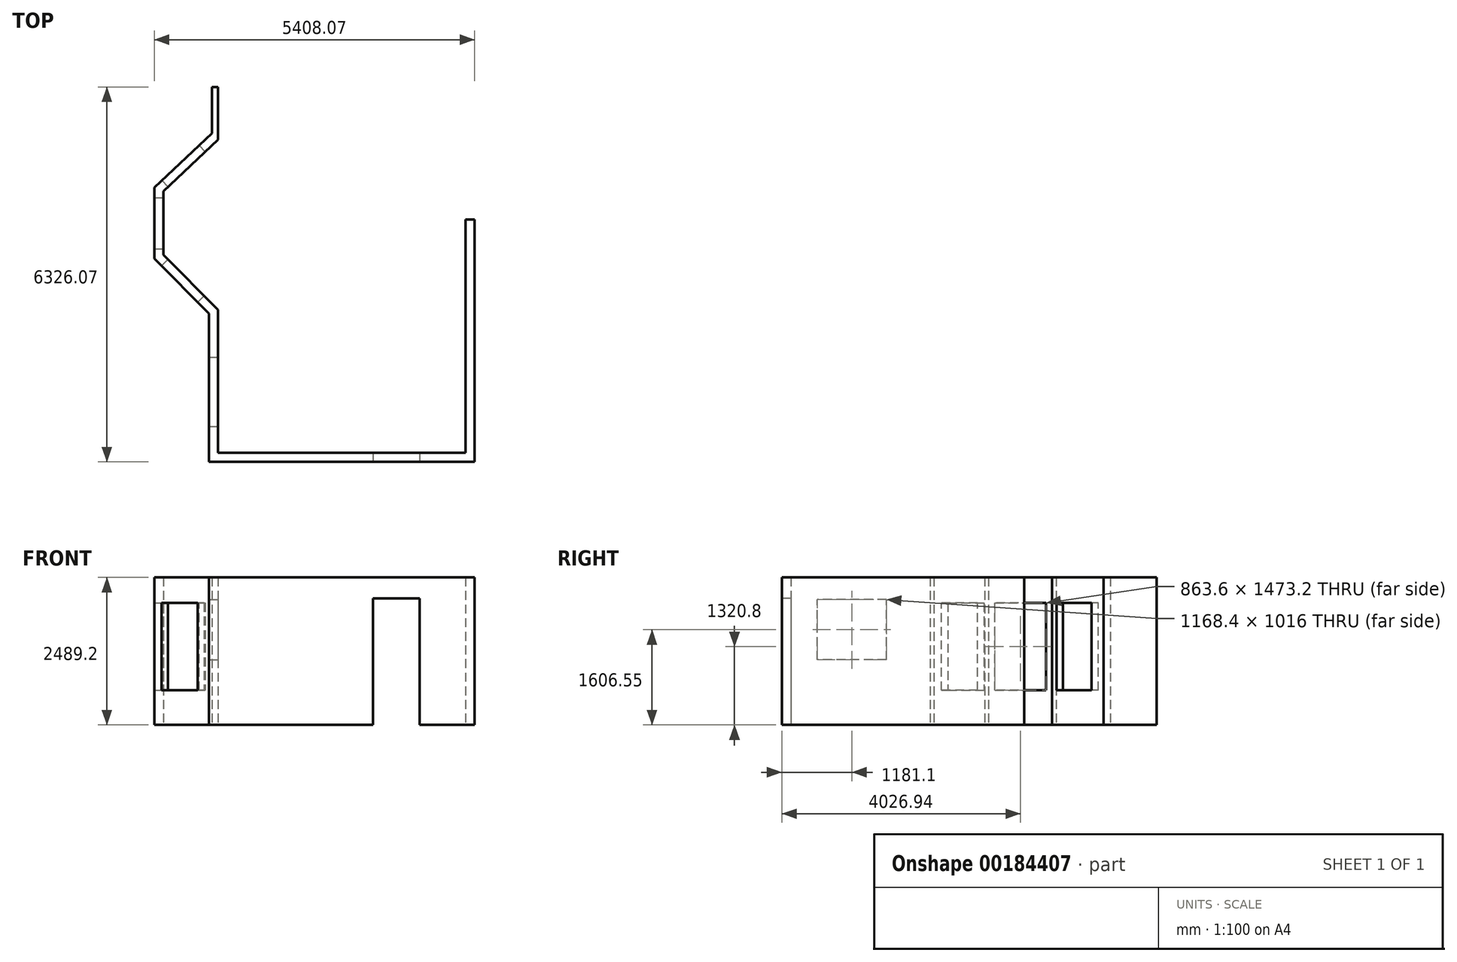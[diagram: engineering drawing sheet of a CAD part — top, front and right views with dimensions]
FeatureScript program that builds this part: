
annotation { "Feature Type Name" : "Feature", "Feature Type Description" : "" }
export const myFeature = defineFeature(function(context is Context, id is Id, definition is map)
    precondition{}
    {
        {
            var Q0;
            Q0=qCreatedBy(makeId("Top.planeOp"),FACE);
            var sketch = newSketch(context, id + "F0", { "sketchPlane" : qUnion([Q0])});
            skLineSegment(sketch, "E0.bottom", {"start": v(0, 0) * mm, "end": v(4178.3, 0) * mm});
            skLineSegment(sketch, "E0.left", {"start": v(0, 0) * mm, "end": v(0, 2413) * mm});
            skLineSegment(sketch, "E0.right", {"start": v(4178.3, 0) * mm, "end": v(4178.3, 3937) * mm});
            skLineSegment(sketch, "E1", {"start": v(0, 2413) * mm, "end": v(-924.97, 3337.97) * mm});
            skLineSegment(sketch, "E2", {"start": v(-924.97, 3337.97) * mm, "end": v(-924.97, 4411.12) * mm});
            skLineSegment(sketch, "E3", {"start": v(-924.97, 4411.12) * mm, "end": v(0, 5281.37) * mm});
            skLineSegment(sketch, "E4.0", {"start": v(-1077.37, 4476.98) * mm, "end": v(-104.43, 5392.36) * mm});
            skLineSegment(sketch, "E4.1", {"start": v(-1077.37, 3274.84) * mm, "end": v(-1077.37, 4476.98) * mm});
            skLineSegment(sketch, "E4.2", {"start": v(4330.7, -152.4) * mm, "end": v(4330.7, 3937) * mm});
            skLineSegment(sketch, "E4.3", {"start": v(-152.4, -152.4) * mm, "end": v(4330.7, -152.4) * mm});
            skLineSegment(sketch, "E4.4", {"start": v(-152.4, -152.4) * mm, "end": v(-152.4, 2349.87) * mm});
            skLineSegment(sketch, "E4.5", {"start": v(-152.4, 2349.87) * mm, "end": v(-1077.37, 3274.84) * mm});
            skLineSegment(sketch, "E5", {"start": v(-104.43, 5392.36) * mm, "end": v(-104.43, 6173.67) * mm});
            skLineSegment(sketch, "E6", {"start": v(-104.43, 6173.67) * mm, "end": v(0, 6173.67) * mm});
            skLineSegment(sketch, "E7", {"start": v(0, 6173.67) * mm, "end": v(0, 5281.37) * mm});
            skLineSegment(sketch, "E8", {"start": v(4178.3, 3937) * mm, "end": v(4330.7, 3937) * mm});
            skSolve(sketch);
        }
        {
            var Q0;
            Q0=qSketchRegion(id+"F0",true);
            extrude(context, id + "F1", {"entities" : qUnion([Q0]), "depth" : 2489.2 * mm});
        }
        {
            var Q0;
            Q0=makeQuery(id+"F1.opExtrude","SWEPT_FACE",FACE,{"disambiguationData":[OSD([sQuery(id+"F0.wireOp",EDGE,"E4.3")])]});
            var sketch = newSketch(context, id + "F2", { "sketchPlane" : qUnion([Q0])});
            skLineSegment(sketch, "E9.bottom", {"start": v(3403.6, 0) * mm, "end": v(2616.2, 0) * mm});
            skLineSegment(sketch, "E9.top", {"start": v(3403.6, 2133.6) * mm, "end": v(2616.2, 2133.6) * mm});
            skLineSegment(sketch, "E9.left", {"start": v(3403.6, 0) * mm, "end": v(3403.6, 2133.6) * mm});
            skLineSegment(sketch, "E9.right", {"start": v(2616.2, 0) * mm, "end": v(2616.2, 2133.6) * mm});
            skSolve(sketch);
        }
        {
            var Q0;
            Q0=qSketchRegion(id+"F2",true);
            extrude(context, id + "F3", {"entities" : qUnion([Q0]), "operationType" : NewBodyOperationType.REMOVE, "oppositeDirection" : true, "depth" : 177.8 * mm});
        }
        {
            var Q0;
            Q0=makeQuery(id+"F1.opExtrude","SWEPT_FACE",FACE,{"disambiguationData":[OSD([sQuery(id+"F0.wireOp",EDGE,"E0.left")])]});
            var sketch = newSketch(context, id + "F4", { "sketchPlane" : qUnion([Q0])});
            skLineSegment(sketch, "E10.bottom", {"start": v(444.5, 2114.55) * mm, "end": v(1612.9, 2114.55) * mm});
            skLineSegment(sketch, "E10.top", {"start": v(444.5, 1098.55) * mm, "end": v(1612.9, 1098.55) * mm});
            skLineSegment(sketch, "E10.left", {"start": v(444.5, 2114.55) * mm, "end": v(444.5, 1098.55) * mm});
            skLineSegment(sketch, "E10.right", {"start": v(1612.9, 2114.55) * mm, "end": v(1612.9, 1098.55) * mm});
            skSolve(sketch);
        }
        {
            var Q0;
            Q0=qSketchRegion(id+"F4",true);
            extrude(context, id + "F5", {"entities" : qUnion([Q0]), "operationType" : NewBodyOperationType.REMOVE, "oppositeDirection" : true, "depth" : 177.8 * mm});
        }
        {
            var Q0;
            Q0=makeQuery(id+"F1.opExtrude","SWEPT_FACE",FACE,{"disambiguationData":[OSD([sQuery(id+"F0.wireOp",EDGE,"E2")])]});
            var sketch = newSketch(context, id + "F6", { "sketchPlane" : qUnion([Q0])});
            skLineSegment(sketch, "E11.bottom", {"start": v(3442.74, 2057.4) * mm, "end": v(4306.34, 2057.4) * mm});
            skLineSegment(sketch, "E11.top", {"start": v(3442.74, 584.2) * mm, "end": v(4306.34, 584.2) * mm});
            skLineSegment(sketch, "E11.left", {"start": v(3442.74, 2057.4) * mm, "end": v(3442.74, 584.2) * mm});
            skLineSegment(sketch, "E11.right", {"start": v(4306.34, 2057.4) * mm, "end": v(4306.34, 584.2) * mm});
            skLineSegment(sketch, "E12", {"start": v(3874.54, 2489.2) * mm, "end": v(3874.54, 0) * mm, "construction": true});
            skSolve(sketch);
        }
        {
            var Q0;
            Q0=qSketchRegion(id+"F6",true);
            extrude(context, id + "F7", {"entities" : qUnion([Q0]), "operationType" : NewBodyOperationType.REMOVE, "oppositeDirection" : true, "depth" : 177.8 * mm});
        }
        {
            var Q0;
            Q0=makeQuery(id+"F1.opExtrude","SWEPT_FACE",FACE,{"disambiguationData":[OSD([sQuery(id+"F0.wireOp",EDGE,"E3")])]});
            var sketch = newSketch(context, id + "F8", { "sketchPlane" : qUnion([Q0])});
            skLineSegment(sketch, "E13.bottom", {"start": v(2456.94, 2057.4) * mm, "end": v(3320.54, 2057.4) * mm});
            skLineSegment(sketch, "E13.top", {"start": v(2456.94, 584.2) * mm, "end": v(3320.54, 584.2) * mm});
            skLineSegment(sketch, "E13.left", {"start": v(2456.94, 2057.4) * mm, "end": v(2456.94, 584.2) * mm});
            skLineSegment(sketch, "E13.right", {"start": v(3320.54, 2057.4) * mm, "end": v(3320.54, 584.2) * mm});
            skSolve(sketch);
        }
        {
            var Q0;
            Q0=qSketchRegion(id+"F8",true);
            extrude(context, id + "F9", {"entities" : qUnion([Q0]), "operationType" : NewBodyOperationType.REMOVE, "oppositeDirection" : true, "depth" : 177.8 * mm});
        }
        {
            var Q0;
            Q0=makeQuery(id+"F1.opExtrude","SWEPT_FACE",FACE,{"disambiguationData":[OSD([sQuery(id+"F0.wireOp",EDGE,"E1")])]});
            var sketch = newSketch(context, id + "F10", { "sketchPlane" : qUnion([Q0])});
            skLineSegment(sketch, "E14.bottom", {"start": v(2042.8, 2057.4) * mm, "end": v(2906.4, 2057.4) * mm});
            skLineSegment(sketch, "E14.top", {"start": v(2042.8, 584.2) * mm, "end": v(2906.4, 584.2) * mm});
            skLineSegment(sketch, "E14.left", {"start": v(2042.8, 2057.4) * mm, "end": v(2042.8, 584.2) * mm});
            skLineSegment(sketch, "E14.right", {"start": v(2906.4, 2057.4) * mm, "end": v(2906.4, 584.2) * mm});
            skSolve(sketch);
        }
        {
            var Q0;
            Q0=qSketchRegion(id+"F10",true);
            extrude(context, id + "F11", {"entities" : qUnion([Q0]), "operationType" : NewBodyOperationType.REMOVE, "oppositeDirection" : true, "depth" : 177.8 * mm});
        }
    });
